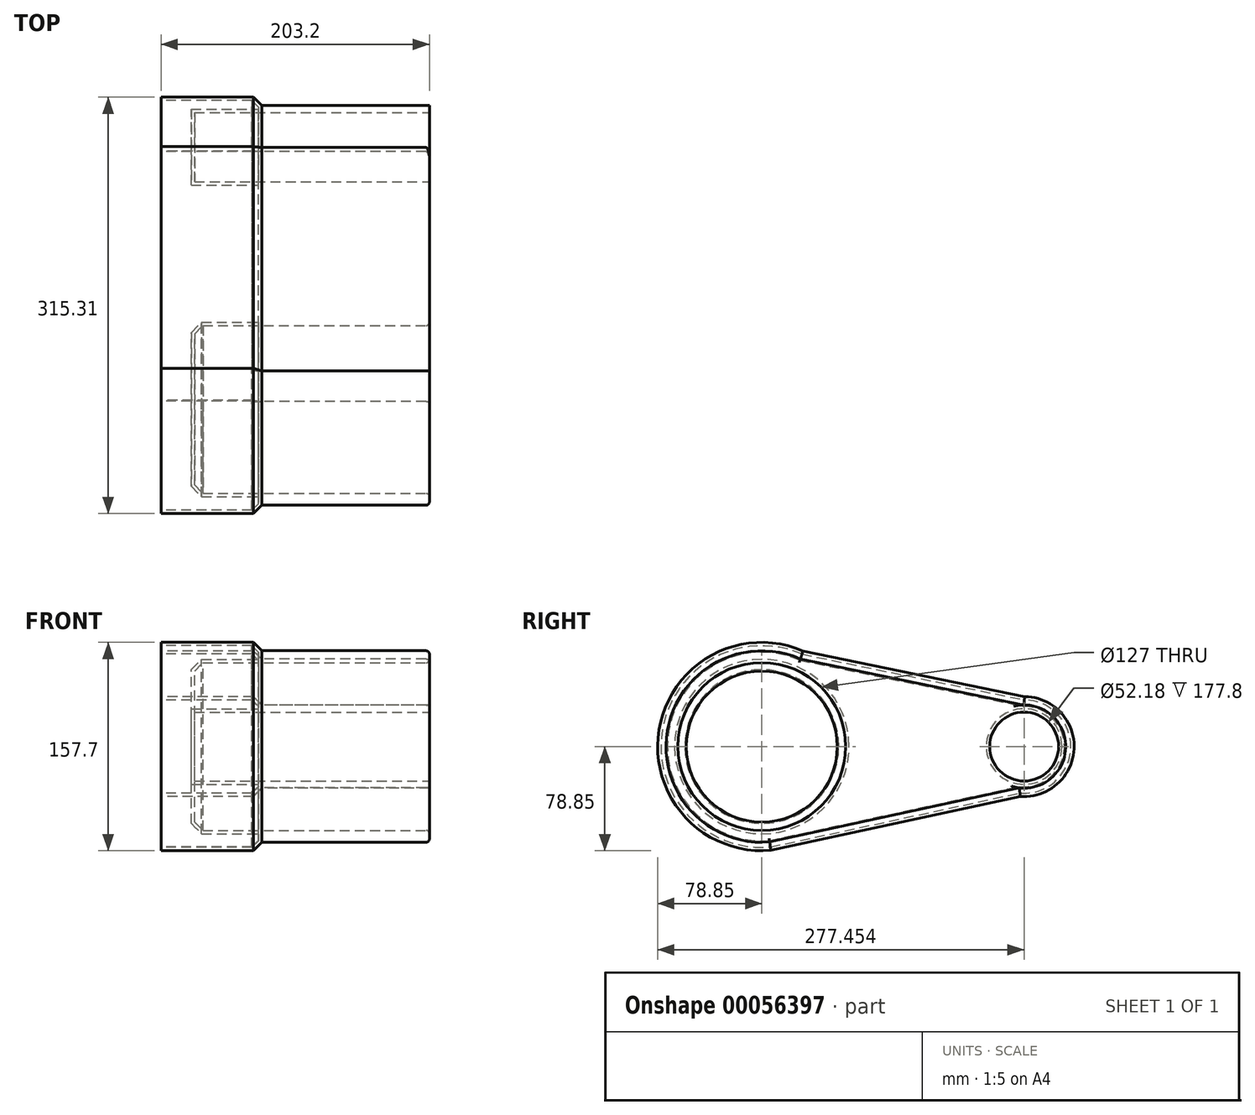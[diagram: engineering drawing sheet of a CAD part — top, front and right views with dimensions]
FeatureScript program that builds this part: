
annotation { "Feature Type Name" : "Feature", "Feature Type Description" : "" }
export const myFeature = defineFeature(function(context is Context, id is Id, definition is map)
    precondition{}
    {
        {
            var Q0;
            Q0=qCreatedBy(makeId("Right.planeOp"),FACE);
            var sketch = newSketch(context, id + "F0", { "sketchPlane" : qUnion([Q0])});
            skCircle(sketch, "E0", {"center": v(0, 0) * mm, "radius": 78.85 * mm});
            skCircle(sketch, "E1", {"center": v(198.6, 0) * mm, "radius": 37.85 * mm});
            skLineSegment(sketch, "E2", {"start": v(31.17, 72.43) * mm, "end": v(199.02, 37.85) * mm});
            skLineSegment(sketch, "E3", {"start": v(6.89, -78.55) * mm, "end": v(195.53, -37.73) * mm});
            skPoint(sketch, "E4.orphan", {"position": v(0, 78.85) * mm});
            skSolve(sketch);
        }
        {
            var Q0;
            {var subQ0=sQuery(id+"F0.wireOp",EDGE,"E0");var subQ1=makeQuery(id+"F0.imprint","INTERSECT",VERTEX,{"derivedFrom":[subQ0,sQuery(id+"F0.wireOp",EDGE,"E2")]});Q0=makeQuery(id+"F0.imprint","IMPRINT",FACE,{"disambiguationData":[TD([[makeQuery(id+"F0.imprint","IMPRINT",EDGE,{"disambiguationData":[TD([[subQ1,-1.0]])],"derivedFrom":subQ0}),1.0]])]});}
            var Q1;
            {var subQ0=sQuery(id+"F0.wireOp",EDGE,"E2");Q1=makeQuery(id+"F0.imprint","IMPRINT",FACE,{"disambiguationData":[TD([[makeQuery(id+"F0.imprint","IMPRINT",EDGE,{"derivedFrom":subQ0}),-1.0]])]});}
            var Q2;
            {var subQ0=sQuery(id+"F0.wireOp",EDGE,"E1");var subQ1=makeQuery(id+"F0.imprint","INTERSECT",VERTEX,{"derivedFrom":[subQ0,sQuery(id+"F0.wireOp",EDGE,"E2")]});Q2=makeQuery(id+"F0.imprint","IMPRINT",FACE,{"disambiguationData":[TD([[makeQuery(id+"F0.imprint","IMPRINT",EDGE,{"disambiguationData":[TD([[subQ1,-1.0]])],"derivedFrom":subQ0}),1.0]])]});}
            extrude(context, id + "F1", {"entities" : qUnion([Q0, Q1, Q2]), "depth" : 76.2 * mm});
        }
        {
            var Q0;
            Q0=makeQuery(id+"F1.opExtrude","CAP_FACE",FACE,{"disambiguationData":[OSD([sQuery(id+"F0.wireOp",EDGE,"E0"),sQuery(id+"F0.wireOp",EDGE,"E1"),sQuery(id+"F0.wireOp",EDGE,"E2"),sQuery(id+"F0.wireOp",EDGE,"E3")])],"isStart":false});
            var sketch = newSketch(context, id + "F2", { "sketchPlane" : qUnion([Q0])});
            skCircle(sketch, "E5", {"center": v(0, 0) * mm, "radius": 63.5 * mm});
            skCircle(sketch, "E6", {"center": v(198.6, 0) * mm, "radius": 26.1 * mm});
            skSolve(sketch);
        }
        {
            var Q0;
            Q0=makeQuery(id+"F2.imprint","IMPRINT",FACE,{"disambiguationData":[TD([[makeQuery(id+"F2.imprint","IMPRINT",EDGE,{"derivedFrom":sQuery(id+"F2.wireOp",EDGE,"E5")}),1.0]])]});
            var Q1;
            Q1=makeQuery(id+"F2.imprint","IMPRINT",FACE,{"disambiguationData":[TD([[makeQuery(id+"F2.imprint","IMPRINT",EDGE,{"derivedFrom":sQuery(id+"F2.wireOp",EDGE,"E6")}),1.0]])]});
            extrude(context, id + "F3", {"entities" : qUnion([Q0, Q1]), "operationType" : NewBodyOperationType.REMOVE, "oppositeDirection" : true, "depth" : 50.8 * mm});
        }
        {
            var Q0;
            Q0=makeQuery(id+"F3.boolean.opBoolean","COPY",EDGE,{"derivedFrom":makeQuery(id+"F3.opExtrude","CAP_EDGE",EDGE,{"disambiguationData":[OSD([sQuery(id+"F2.wireOp",EDGE,"E5")])],"isStart":true})});
            var Q1;
            Q1=makeQuery(id+"F3.boolean.opBoolean","COPY",EDGE,{"derivedFrom":makeQuery(id+"F3.opExtrude","CAP_EDGE",EDGE,{"disambiguationData":[OSD([sQuery(id+"F2.wireOp",EDGE,"E6")])],"isStart":true})});
            var Q2;
            Q2=makeQuery(id+"F1.opExtrude","CAP_EDGE",EDGE,{"disambiguationData":[OSD([sQuery(id+"F0.wireOp",EDGE,"E2")])],"isStart":false});
            var Q3;
            Q3=makeQuery(id+"F1.opExtrude","CAP_EDGE",EDGE,{"disambiguationData":[OSD([sQuery(id+"F0.wireOp",EDGE,"E3")])],"isStart":false});
            var Q4;
            Q4=makeQuery(id+"F3.boolean.opBoolean","COPY",EDGE,{"derivedFrom":makeQuery(id+"F3.opExtrude","CAP_EDGE",EDGE,{"disambiguationData":[OSD([sQuery(id+"F2.wireOp",EDGE,"E5")])],"isStart":false})});
            var Q5;
            Q5=makeQuery(id+"F1.opExtrude","CAP_EDGE",EDGE,{"disambiguationData":[OSD([sQuery(id+"F0.wireOp",EDGE,"E0")])],"isStart":false});
            var Q6;
            Q6=makeQuery(id+"F1.opExtrude","CAP_EDGE",EDGE,{"disambiguationData":[OSD([sQuery(id+"F0.wireOp",EDGE,"E1")])],"isStart":false});
            chamfer(context, id + "F4", {"entities" : qUnion([Q0, Q1, Q2, Q3, Q4, Q5, Q6]), "width" : 6.35 * mm, "tangentPropagation" : true});
        }
        {
            var Q0;
            Q0=makeQuery(id+"F1.opExtrude","CAP_FACE",FACE,{"disambiguationData":[OSD([sQuery(id+"F0.wireOp",EDGE,"E0"),sQuery(id+"F0.wireOp",EDGE,"E1"),sQuery(id+"F0.wireOp",EDGE,"E2"),sQuery(id+"F0.wireOp",EDGE,"E3")])],"isStart":true});
            shell(context, id + "F5", {"entities" : qUnion([Q0]), "thickness" : 2.54 * mm});
        }
        {
            var Q0;
            Q0=makeQuery(id+"F1.opExtrude","CAP_FACE",FACE,{"disambiguationData":[OSD([sQuery(id+"F0.wireOp",EDGE,"E0"),sQuery(id+"F0.wireOp",EDGE,"E1"),sQuery(id+"F0.wireOp",EDGE,"E2"),sQuery(id+"F0.wireOp",EDGE,"E3")])],"isStart":false});
            extrude(context, id + "F6", {"entities" : qUnion([Q0]), "operationType" : NewBodyOperationType.ADD, "depth" : 127 * mm});
        }
        {
            var Q0;
            {var subQ0=sQuery(id+"F0.wireOp",EDGE,"E3");var subQ1=sQuery(id+"F0.wireOp",EDGE,"E2");var subQ2=sQuery(id+"F0.wireOp",EDGE,"E1");var subQ3=sQuery(id+"F0.wireOp",EDGE,"E0");Q0=makeQuery(id+"F6.opExtrude","CAP_EDGE",EDGE,{"disambiguationData":[OSD([subQ3,subQ2,subQ1,subQ0]),TDD([makeQuery(id+"F4.opChamfer","BLEND_EDGE",EDGE,{"blendedFrom":[makeQuery(id+"F1.opExtrude","CAP_EDGE",EDGE,{"disambiguationData":[OSD([subQ0])],"isStart":false}),makeQuery(id+"F1.opExtrude","CAP_FACE",FACE,{"disambiguationData":[OSD([subQ3,subQ2,subQ1,subQ0])],"isStart":false})],"blendedInto":[makeQuery(id+"F1.opExtrude","CAP_FACE",FACE,{"disambiguationData":[OSD([subQ3,subQ2,subQ1,subQ0])],"isStart":false})]})])],"isStart":false});}
            var Q1;
            {var subQ0=sQuery(id+"F0.wireOp",EDGE,"E3");var subQ1=sQuery(id+"F0.wireOp",EDGE,"E2");var subQ2=sQuery(id+"F0.wireOp",EDGE,"E1");var subQ3=sQuery(id+"F0.wireOp",EDGE,"E0");Q1=makeQuery(id+"F6.opExtrude","CAP_EDGE",EDGE,{"disambiguationData":[OSD([subQ3,subQ2,subQ1,subQ0]),TDD([makeQuery(id+"F4.opChamfer","BLEND_EDGE",EDGE,{"blendedFrom":[makeQuery(id+"F1.opExtrude","CAP_EDGE",EDGE,{"disambiguationData":[OSD([subQ1])],"isStart":false}),makeQuery(id+"F1.opExtrude","CAP_FACE",FACE,{"disambiguationData":[OSD([subQ3,subQ2,subQ1,subQ0])],"isStart":false})],"blendedInto":[makeQuery(id+"F1.opExtrude","CAP_FACE",FACE,{"disambiguationData":[OSD([subQ3,subQ2,subQ1,subQ0])],"isStart":false})]})])],"isStart":false});}
            var Q2;
            Q2=makeQuery(id+"F6.opExtrude","CAP_EDGE",EDGE,{"disambiguationData":[OSD([sQuery(id+"F0.wireOp",EDGE,"E0"),sQuery(id+"F0.wireOp",EDGE,"E1"),sQuery(id+"F0.wireOp",EDGE,"E2"),sQuery(id+"F0.wireOp",EDGE,"E3"),sQuery(id+"F2.wireOp",EDGE,"E5")])],"isStart":false});
            var Q3;
            {var subQ0=sQuery(id+"F0.wireOp",EDGE,"E3");var subQ1=sQuery(id+"F0.wireOp",EDGE,"E2");var subQ2=sQuery(id+"F0.wireOp",EDGE,"E1");var subQ3=sQuery(id+"F0.wireOp",EDGE,"E0");Q3=makeQuery(id+"F6.opExtrude","CAP_EDGE",EDGE,{"disambiguationData":[OSD([subQ3,subQ2,subQ1,subQ0]),TDD([makeQuery(id+"F4.opChamfer","BLEND_EDGE",EDGE,{"blendedFrom":[makeQuery(id+"F1.opExtrude","CAP_EDGE",EDGE,{"disambiguationData":[OSD([subQ3])],"isStart":false}),makeQuery(id+"F1.opExtrude","CAP_FACE",FACE,{"disambiguationData":[OSD([subQ3,subQ2,subQ1,subQ0])],"isStart":false})],"blendedInto":[makeQuery(id+"F1.opExtrude","CAP_FACE",FACE,{"disambiguationData":[OSD([subQ3,subQ2,subQ1,subQ0])],"isStart":false})]})])],"isStart":false});}
            fillet(context, id + "F7", {"entities" : qUnion([Q0, Q1, Q2, Q3]), "radius" : 2.54 * mm, "tangentPropagation" : true, "allowEdgeOverflow" : false});
        }
    });
